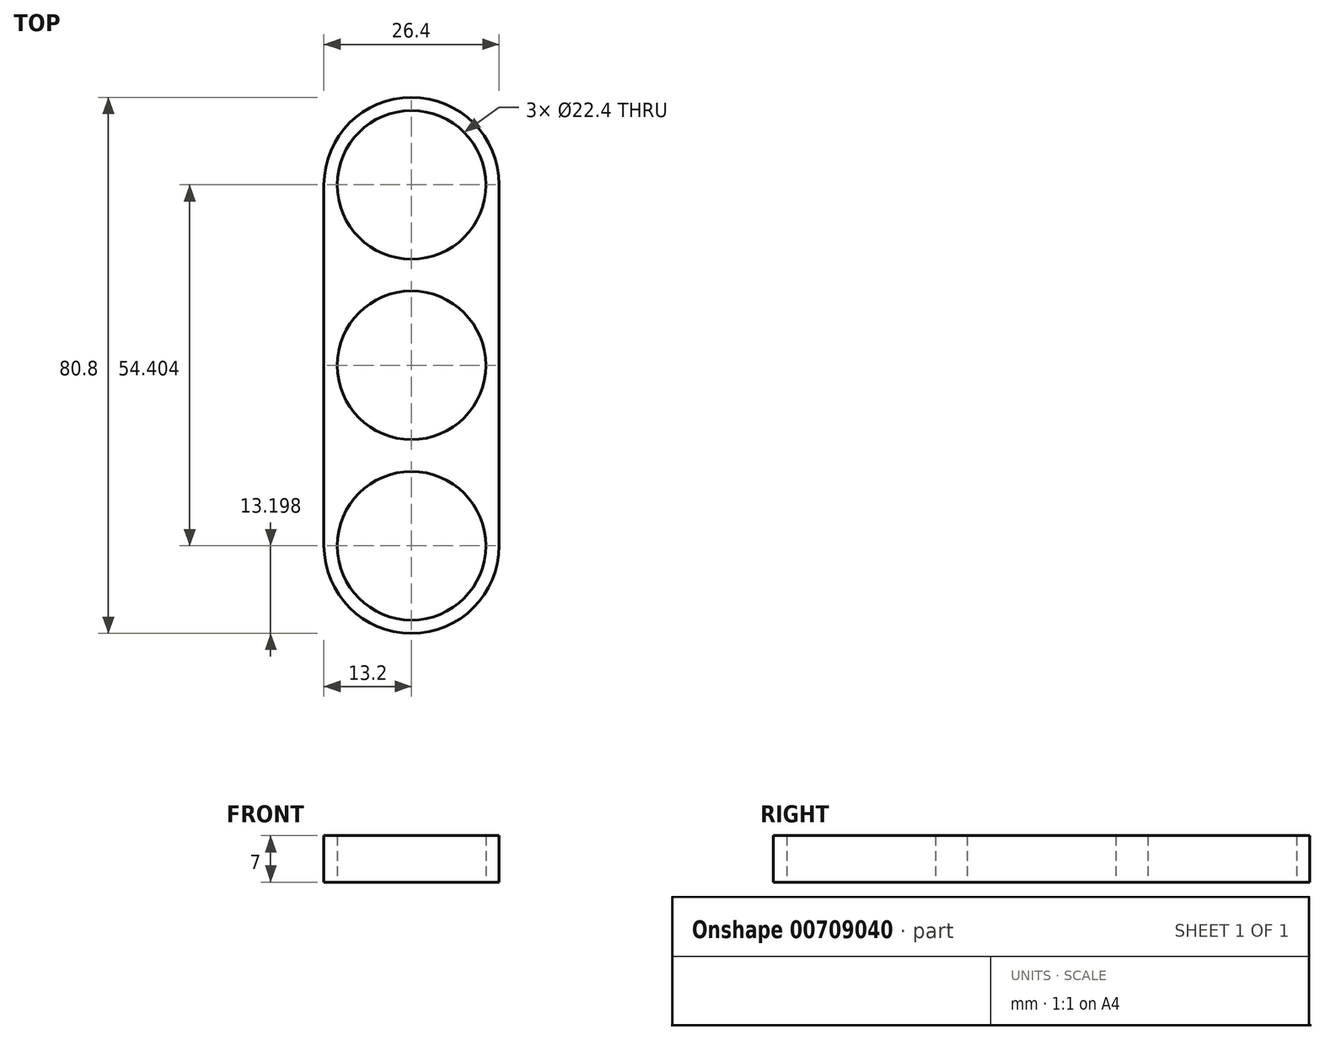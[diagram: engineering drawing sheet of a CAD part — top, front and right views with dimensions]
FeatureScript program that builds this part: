
annotation { "Feature Type Name" : "Feature", "Feature Type Description" : "" }
export const myFeature = defineFeature(function(context is Context, id is Id, definition is map)
    precondition{}
    {
        {
            var Q0;
            Q0=qCreatedBy(makeId("Top.planeOp"),FACE);
            var sketch = newSketch(context, id + "F0", { "sketchPlane" : qUnion([Q0])});
            skCircle(sketch, "E0", {"center": v(0, 0) * mm, "radius": 11.2 * mm});
            skCircle(sketch, "E1", {"center": v(0, 27.2) * mm, "radius": 11.2 * mm});
            skArc(sketch, "E2", {"start": v(13.2, 27.2) * mm, "mid": v(0, 40.4) * mm, "end": v(-13.2, 27.2) * mm});
            skCircle(sketch, "E3.1.0", {"center": v(0, -27.2) * mm, "radius": 11.2 * mm});
            skArc(sketch, "E3.1.1", {"start": v(-13.2, -27.2) * mm, "mid": v(0, -40.4) * mm, "end": v(13.2, -27.2) * mm});
            skLineSegment(sketch, "E4", {"start": v(13.2, 27.2) * mm, "end": v(13.2, -27.2) * mm});
            skLineSegment(sketch, "E5", {"start": v(-13.2, 27.2) * mm, "end": v(-13.2, -27.2) * mm});
            skSolve(sketch);
        }
        {
            var Q0;
            Q0 = qSketchRegion(id + "F0", true);
            extrude(context, id + "F1", {"entities" : qUnion([Q0]), "depth" : 7 * mm, "offsetDistance" : 25 * mm});
        }
    });
